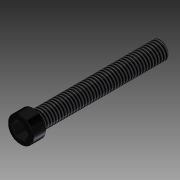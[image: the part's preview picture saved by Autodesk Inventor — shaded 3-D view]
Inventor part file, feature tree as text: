
AUTODESK INVENTOR PART (.ipt)
format: ipt  version: 2013 (Build 170138000, 138)  size: 108,544 bytes
history: native  units: in
note: dims shown in document units (in); Inventor stores cm internally (conversion verified against a paired STEP export)
features: extrude x3, sketch x1, thread x1, chamfer x1
ambient origin geometry x8: Origin, YZ Plane, XZ Plane, XY Plane, X Axis, Y Axis, Z Axis, Center Point
bodies: Solid1 (feature_tree)
feature tree (6):
  sketch  "Sketch1"  dims[d0=0.275in d1=0.185in d2=0.15in d3=0.15in d4=0.0in d5=1.35in d6=0.0in d7=0.05in d8=0.0in d9=1.0in d10=0.0in d11=0.01in d12=0.125in d13=45.0deg]
  extrude  "Extrusion1"  Depth=0.185in
  extrude  "Extrusion2"  Depth=0.15in
  extrude  "Extrusion3"  Depth=0.15in TaperAngle=0.0deg
  thread  "Thread1"  [1 undecoded]
  chamfer  "Chamfer1"  Distance=0.05in
note: 1 required parameter value undecoded (feature->parameter linkage not recoverable at this tier; creation-order binding heuristic only, values carry confidence <= 0.55)
